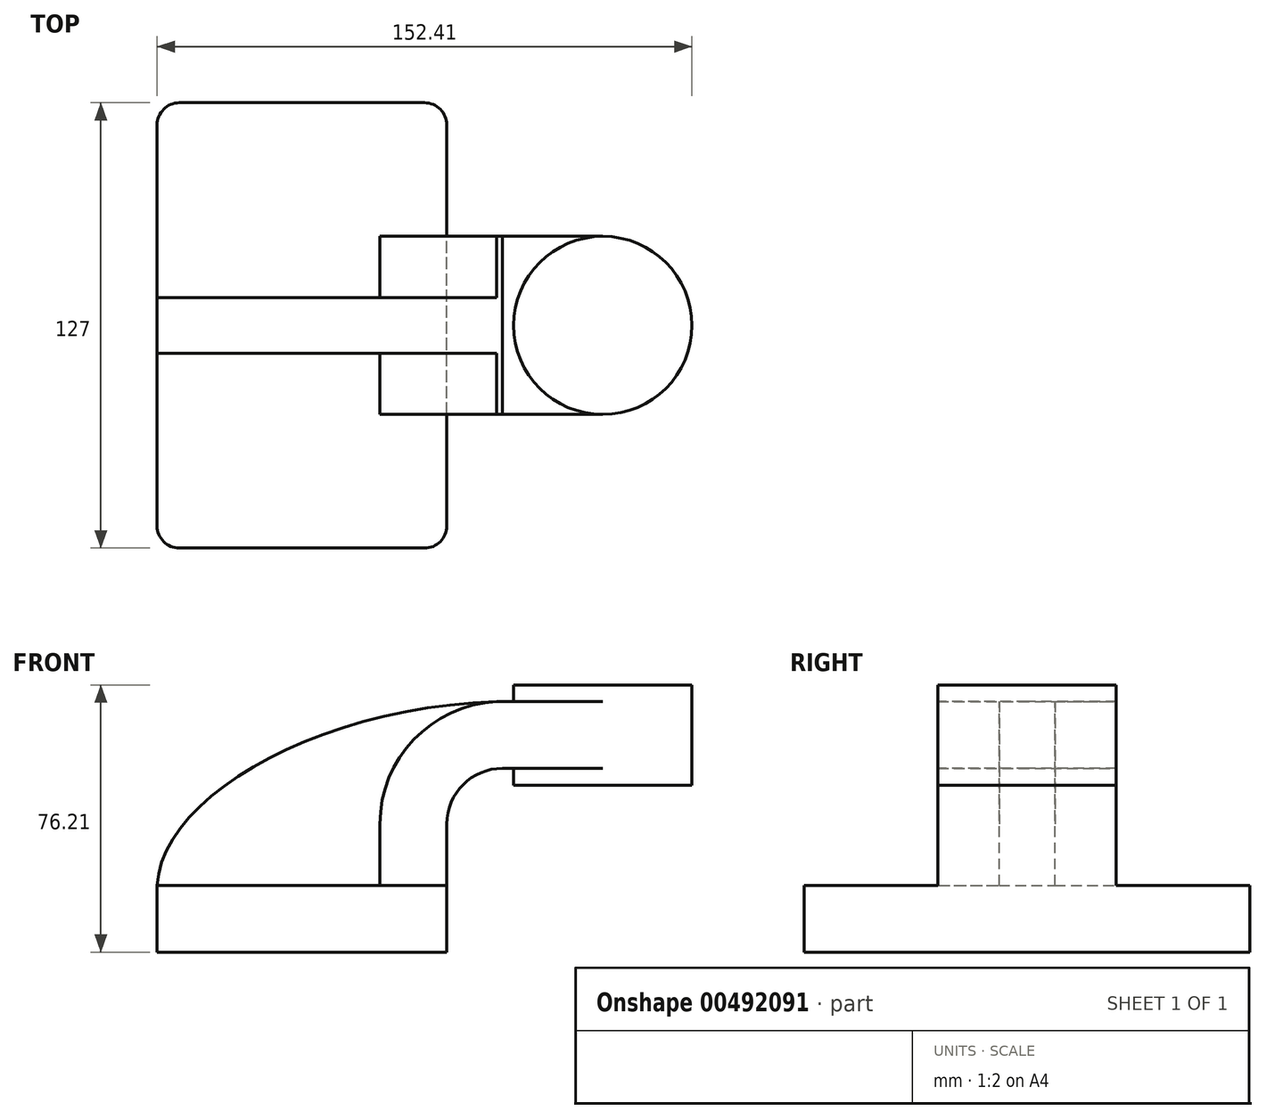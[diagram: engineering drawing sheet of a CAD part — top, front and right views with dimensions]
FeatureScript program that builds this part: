
annotation { "Feature Type Name" : "Feature", "Feature Type Description" : "" }
export const myFeature = defineFeature(function(context is Context, id is Id, definition is map)
    precondition{}
    {
        {
            var Q0;
            Q0=qCreatedBy(makeId("Front.planeOp"),FACE);
            var sketch = newSketch(context, id + "F0", { "sketchPlane" : qUnion([Q0])});
            skLineSegment(sketch, "E0.bottom", {"start": v(41.27, 9.53) * mm, "end": v(-41.28, 9.53) * mm});
            skLineSegment(sketch, "E0.top", {"start": v(41.28, -9.52) * mm, "end": v(-41.27, -9.52) * mm});
            skLineSegment(sketch, "E0.left", {"start": v(41.28, 9.53) * mm, "end": v(41.28, -9.52) * mm});
            skLineSegment(sketch, "E0.right", {"start": v(-41.28, 9.53) * mm, "end": v(-41.28, -9.52) * mm});
            skPoint(sketch, "E0.middle", {"position": v(0, 0) * mm});
            skLineSegment(sketch, "E1.bottom", {"start": v(60.32, 38.1) * mm, "end": v(111.12, 38.1) * mm});
            skLineSegment(sketch, "E1.top", {"start": v(60.32, 66.68) * mm, "end": v(111.12, 66.68) * mm});
            skLineSegment(sketch, "E1.left", {"start": v(60.32, 38.1) * mm, "end": v(60.32, 66.68) * mm});
            skLineSegment(sketch, "E1.right", {"start": v(111.12, 38.1) * mm, "end": v(111.12, 66.68) * mm});
            skPoint(sketch, "E1.middle", {"position": v(85.72, 52.39) * mm});
            skLineSegment(sketch, "E2", {"start": v(41.27, 9.53) * mm, "end": v(41.27, 27) * mm});
            skArc(sketch, "E3", {"start": v(41.27, 27) * mm, "mid": v(45.92, 38.23) * mm, "end": v(57.15, 42.88) * mm});
            skLineSegment(sketch, "E4", {"start": v(57.15, 42.88) * mm, "end": v(85.72, 42.88) * mm});
            skLineSegment(sketch, "E5.0", {"start": v(57.15, 61.93) * mm, "end": v(85.72, 61.93) * mm});
            skArc(sketch, "E5.1", {"start": v(22.22, 27) * mm, "mid": v(32.45, 51.7) * mm, "end": v(57.15, 61.93) * mm});
            skLineSegment(sketch, "E5.2", {"start": v(22.22, 9.53) * mm, "end": v(22.22, 27) * mm});
            skPoint(sketch, "E6.startSnap0", {"position": v(85.72, 66.68) * mm});
            skLineSegment(sketch, "E7", {"start": v(85.72, 38.1) * mm, "end": v(85.72, 66.68) * mm});
            skFitSpline(sketch, "E8", {"points": [v(-41.28, 9.53) * mm, v(57.15, 61.93) * mm], "startDerivative": vector(3.99, 76.55) * mm, "endDerivative": vector(155.81, 3.01) * mm});
            skSolve(sketch);
        }
        {
            var Q0;
            Q0=makeQuery(id+"F0.imprint","IMPRINT",FACE,{"disambiguationData":[TD([[makeQuery(id+"F0.imprint","IMPRINT",EDGE,{"derivedFrom":sQuery(id+"F0.wireOp",EDGE,"E0.top")}),-1.0]])]});
            extrude(context, id + "F1", {"entities" : qUnion([Q0]), "endBound" : BoundingType.SYMMETRIC, "depth" : 127 * mm});
        }
        {
            var Q0;
            {var subQ1=sQuery(id+"F0.wireOp",EDGE,"E2");Q0=makeQuery(id+"F0.imprint","IMPRINT",FACE,{"disambiguationData":[TD([[makeQuery(id+"F0.imprint","IMPRINT",EDGE,{"derivedFrom":subQ1}),1.0]])]});}
            var Q1;
            {var subQ0=sQuery(id+"F0.wireOp",EDGE,"E4");var subQ1=sQuery(id+"F0.wireOp",EDGE,"E1.left");var subQ2=makeQuery(id+"F0.imprint","INTERSECT",VERTEX,{"derivedFrom":[subQ1,subQ0]});Q1=makeQuery(id+"F0.imprint","IMPRINT",FACE,{"disambiguationData":[TD([[makeQuery(id+"F0.imprint","IMPRINT",EDGE,{"disambiguationData":[TD([[subQ2,-1.0]])],"derivedFrom":subQ1}),-1.0]])]});}
            extrude(context, id + "F2", {"entities" : qUnion([Q0, Q1]), "operationType" : NewBodyOperationType.ADD, "endBound" : BoundingType.SYMMETRIC, "depth" : 50.8 * mm});
        }
        {
            var Q0;
            {var subQ3=sQuery(id+"F0.wireOp",EDGE,"E5.2");Q0=makeQuery(id+"F0.imprint","IMPRINT",FACE,{"disambiguationData":[TD([[makeQuery(id+"F0.imprint","IMPRINT",EDGE,{"derivedFrom":subQ3}),1.0]])]});}
            extrude(context, id + "F3", {"entities" : qUnion([Q0]), "operationType" : NewBodyOperationType.ADD, "endBound" : BoundingType.SYMMETRIC, "depth" : 15.88 * mm});
        }
        {
            var Q0;
            {var subQ4=sQuery(id+"F0.wireOp",EDGE,"E1.right");Q0=makeQuery(id+"F0.imprint","IMPRINT",FACE,{"disambiguationData":[TD([[makeQuery(id+"F0.imprint","IMPRINT",EDGE,{"derivedFrom":subQ4}),1.0]])]});}
            var Q1;
            Q1=sQuery(id+"F0.wireOp",EDGE,"E7");
            revolve(context, id + "F4", {"operationType" : NewBodyOperationType.ADD, "entities" : qUnion([Q0]), "axis" : qUnion([Q1]), "revolveType" : RevolveType.FULL});
        }
        {
            var Q0;
            Q0=makeQuery(id+"F1.opExtrude","CAP_EDGE",EDGE,{"disambiguationData":[OSD([sQuery(id+"F0.wireOp",EDGE,"E0.right")])],"isStart":false});
            var Q1;
            Q1=makeQuery(id+"F1.opExtrude","CAP_EDGE",EDGE,{"disambiguationData":[OSD([sQuery(id+"F0.wireOp",EDGE,"E0.left")])],"isStart":false});
            var Q2;
            Q2=makeQuery(id+"F1.opExtrude","CAP_EDGE",EDGE,{"disambiguationData":[OSD([sQuery(id+"F0.wireOp",EDGE,"E0.left")])],"isStart":true});
            var Q3;
            Q3=makeQuery(id+"F1.opExtrude","CAP_EDGE",EDGE,{"disambiguationData":[OSD([sQuery(id+"F0.wireOp",EDGE,"E0.right")])],"isStart":true});
            fillet(context, id + "F5", {"entities" : qUnion([Q0, Q1, Q2, Q3]), "radius" : 6.35 * mm, "tangentPropagation" : true, "allowEdgeOverflow" : false});
        }
    });
